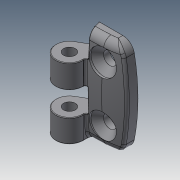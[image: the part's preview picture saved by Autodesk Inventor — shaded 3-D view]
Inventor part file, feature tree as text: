
AUTODESK INVENTOR PART (.ipt)
format: ipt  version: 2018.3 (Build 223284000, 284)  size: 436,736 bytes
history: native  units: in
note: dims shown in document units (in); Inventor stores cm internally (conversion verified against a paired STEP export)
features: mirror x2, revolve x1
ambient origin geometry x8: Origin, YZ Plane, XZ Plane, XY Plane, X Axis, Y Axis, Z Axis, Center Point
bodies: Solid1 (feature_tree), Solid2 (feature_tree), Solid3 (feature_tree)
feature tree (3):
  revolve  "Revolve1"  [1 undecoded]
  mirror  "Mirror3"
  mirror  "Mirror1"
note: 1 required parameter value undecoded (feature->parameter linkage not recoverable at this tier; creation-order binding heuristic only, values carry confidence <= 0.55)
